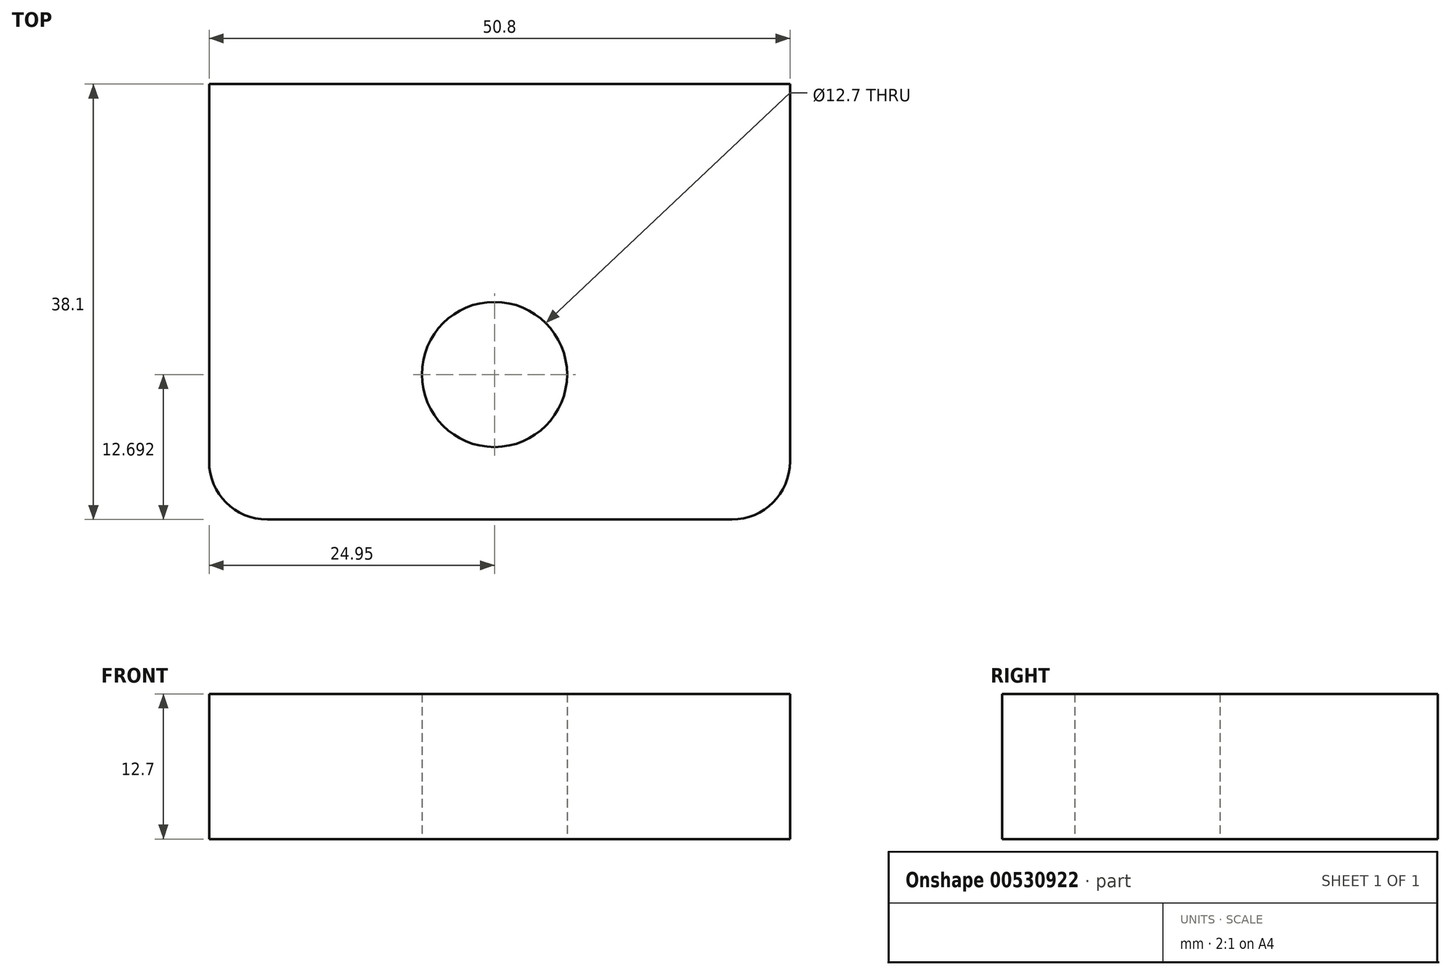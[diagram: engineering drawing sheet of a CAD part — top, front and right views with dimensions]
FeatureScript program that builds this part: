
annotation { "Feature Type Name" : "Feature", "Feature Type Description" : "" }
export const myFeature = defineFeature(function(context is Context, id is Id, definition is map)
    precondition{}
    {
        {
            var Q0;
            Q0=qCreatedBy(makeId("Top.planeOp"),FACE);
            var sketch = newSketch(context, id + "F0", { "sketchPlane" : qUnion([Q0])});
            skLineSegment(sketch, "E0", {"start": v(25.85, 0) * mm, "end": v(-24.95, 0) * mm});
            skLineSegment(sketch, "E1", {"start": v(-24.95, 0) * mm, "end": v(-24.95, -38.1) * mm});
            skLineSegment(sketch, "E2", {"start": v(-24.95, -38.1) * mm, "end": v(25.85, -38.1) * mm});
            skLineSegment(sketch, "E3", {"start": v(25.85, -38.1) * mm, "end": v(25.85, 0) * mm});
            skSolve(sketch);
        }
        {
            var Q0;
            Q0 = qSketchRegion(id + "F0", true);
            extrude(context, id + "F1", {"entities" : qUnion([Q0]), "depth" : 12.7 * mm, "offsetDistance" : 25.4 * mm});
        }
        {
            var Q0;
            Q0=makeQuery(id+"F1.opExtrude","SWEPT_EDGE",EDGE,{"disambiguationData":[OSD([sQuery(id+"F0.wireOp",EDGE,"E1"),sQuery(id+"F0.wireOp",EDGE,"E2")])]});
            var Q1;
            Q1=makeQuery(id+"F1.opExtrude","SWEPT_EDGE",EDGE,{"disambiguationData":[OSD([sQuery(id+"F0.wireOp",EDGE,"E2"),sQuery(id+"F0.wireOp",EDGE,"E3")])]});
            fillet(context, id + "F2", {"entities" : qUnion([Q0, Q1]), "radius" : 5.08 * mm, "tangentPropagation" : true, "allowEdgeOverflow" : false});
        }
        {
            var Q0;
            Q0=qCreatedBy(makeId("Top.planeOp"),FACE);
            var sketch = newSketch(context, id + "F3", { "sketchPlane" : qUnion([Q0])});
            skCircle(sketch, "E4", {"center": v(0, -25.4) * mm, "radius": 6.35 * mm});
            skSolve(sketch);
        }
        {
            var Q0;
            Q0=makeQuery(id+"F3.imprint","IMPRINT",FACE,{"disambiguationData":[TD([[makeQuery(id+"F3.imprint","IMPRINT",EDGE,{"derivedFrom":sQuery(id+"F3.wireOp",EDGE,"E4")}),1.0]])]});
            extrude(context, id + "F4", {"entities" : qUnion([Q0]), "operationType" : NewBodyOperationType.REMOVE, "endBound" : BoundingType.THROUGH_ALL, "depth" : 91.19 * mm, "offsetDistance" : 25.4 * mm});
        }
    });
